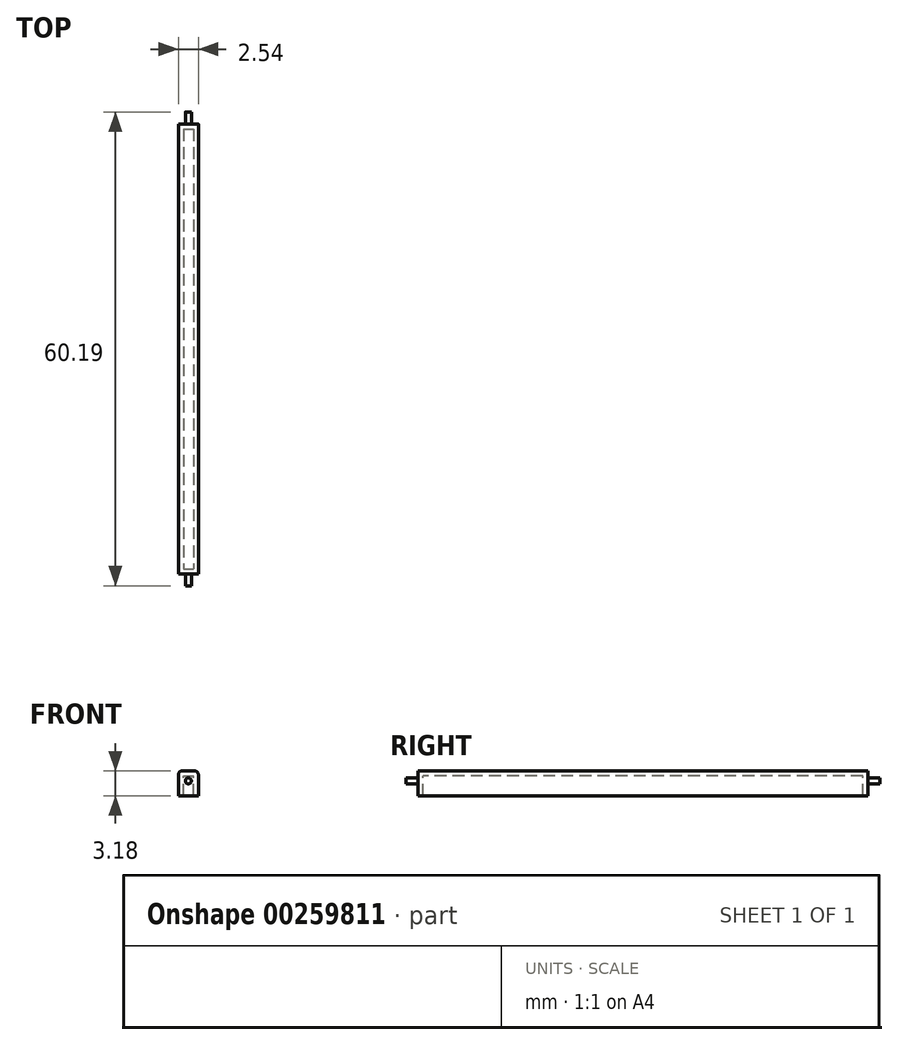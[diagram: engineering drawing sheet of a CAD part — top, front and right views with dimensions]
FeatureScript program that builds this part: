
annotation { "Feature Type Name" : "Feature", "Feature Type Description" : "" }
export const myFeature = defineFeature(function(context is Context, id is Id, definition is map)
    precondition{}
    {
        {
            var Q0;
            Q0=qCreatedBy(makeId("Front.planeOp"),FACE);
            var sketch = newSketch(context, id + "F0", { "sketchPlane" : qUnion([Q0])});
            skLineSegment(sketch, "E0.bottom", {"start": v(-1.27, 0) * mm, "end": v(1.27, 0) * mm});
            skLineSegment(sketch, "E0.top", {"start": v(-0.76, 3.17) * mm, "end": v(0.76, 3.17) * mm});
            skLineSegment(sketch, "E0.left", {"start": v(-1.27, 0) * mm, "end": v(-1.27, 2.67) * mm});
            skLineSegment(sketch, "E0.right", {"start": v(1.27, 0) * mm, "end": v(1.27, 2.67) * mm});
            skPoint(sketch, "E1.visualSharp", {"position": v(-1.27, 3.17) * mm});
            skArc(sketch, "E1.filletArc", {"start": v(-0.76, 3.18) * mm, "mid": v(-1.12, 3.03) * mm, "end": v(-1.27, 2.67) * mm});
            skPoint(sketch, "E2.visualSharp", {"position": v(1.27, 3.17) * mm});
            skArc(sketch, "E2.filletArc", {"start": v(1.27, 2.67) * mm, "mid": v(1.12, 3.03) * mm, "end": v(0.76, 3.18) * mm});
            skSolve(sketch);
        }
        {
            var Q0;
            Q0=qSketchRegion(id+"F0",true);
            extrude(context, id + "F1", {"entities" : qUnion([Q0]), "oppositeDirection" : true, "depth" : 57.15 * mm});
        }
        {
            var Q0;
            Q0=makeQuery(id+"F1.opExtrude","CAP_FACE",FACE,{"disambiguationData":[OSD([sQuery(id+"F0.wireOp",EDGE,"E0.bottom"),sQuery(id+"F0.wireOp",EDGE,"E0.top"),sQuery(id+"F0.wireOp",EDGE,"E0.left"),sQuery(id+"F0.wireOp",EDGE,"E0.right"),sQuery(id+"F0.wireOp",EDGE,"E1.filletArc"),sQuery(id+"F0.wireOp",EDGE,"E2.filletArc")])],"isStart":true});
            var sketch = newSketch(context, id + "F2", { "sketchPlane" : qUnion([Q0])});
            skCircle(sketch, "E3", {"center": v(0, 1.9) * mm, "radius": 0.38 * mm});
            skSolve(sketch);
        }
        {
            var Q0;
            Q0=qSketchRegion(id+"F2",true);
            extrude(context, id + "F3", {"entities" : qUnion([Q0]), "operationType" : NewBodyOperationType.ADD, "depth" : 1.52 * mm});
        }
        {
            var Q0;
            Q0=makeQuery(id+"F1.opExtrude","CAP_FACE",FACE,{"disambiguationData":[OSD([sQuery(id+"F0.wireOp",EDGE,"E0.bottom"),sQuery(id+"F0.wireOp",EDGE,"E0.top"),sQuery(id+"F0.wireOp",EDGE,"E0.left"),sQuery(id+"F0.wireOp",EDGE,"E0.right"),sQuery(id+"F0.wireOp",EDGE,"E1.filletArc"),sQuery(id+"F0.wireOp",EDGE,"E2.filletArc")])],"isStart":false});
            var sketch = newSketch(context, id + "F4", { "sketchPlane" : qUnion([Q0])});
            skCircle(sketch, "E4", {"center": v(0, 1.9) * mm, "radius": 0.38 * mm});
            skSolve(sketch);
        }
        {
            var Q0;
            Q0=qSketchRegion(id+"F4",true);
            extrude(context, id + "F5", {"entities" : qUnion([Q0]), "operationType" : NewBodyOperationType.ADD, "depth" : 1.52 * mm});
        }
        {
            var Q0;
            Q0=makeQuery(id+"F1.opExtrude","SWEPT_FACE",FACE,{"disambiguationData":[OSD([sQuery(id+"F0.wireOp",EDGE,"E0.bottom")])]});
            shell(context, id + "F6", {"entities" : qUnion([Q0]), "thickness" : 0.64 * mm});
        }
    });
